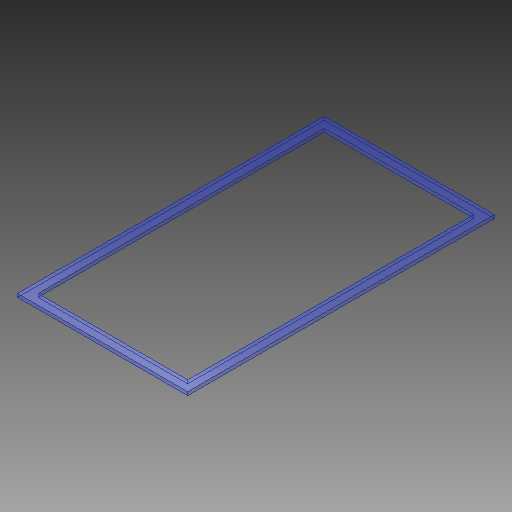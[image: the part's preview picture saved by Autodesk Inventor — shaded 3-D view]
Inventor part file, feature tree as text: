
AUTODESK INVENTOR PART (.ipt)
format: ipt  version: 2018.1 (Build 221171000, 171)  size: 106,496 bytes
history: native  units: mm
features: extrude x1, sketch x1
ambient origin geometry x8: Origin, YZ Plane, XZ Plane, XY Plane, X Axis, Y Axis, Z Axis, Center Point
bodies: Body1 (feature_tree)
feature tree (2):
  extrude  "Extrusion3"  Depth=5.0mm
  sketch  "Sketch1"  dims[d0=260.0mm d1=460.0mm d8=249.0mm d9=449.0mm d10=219.0mm d11=419.0mm d12=5.0mm d13=0.0mm]
